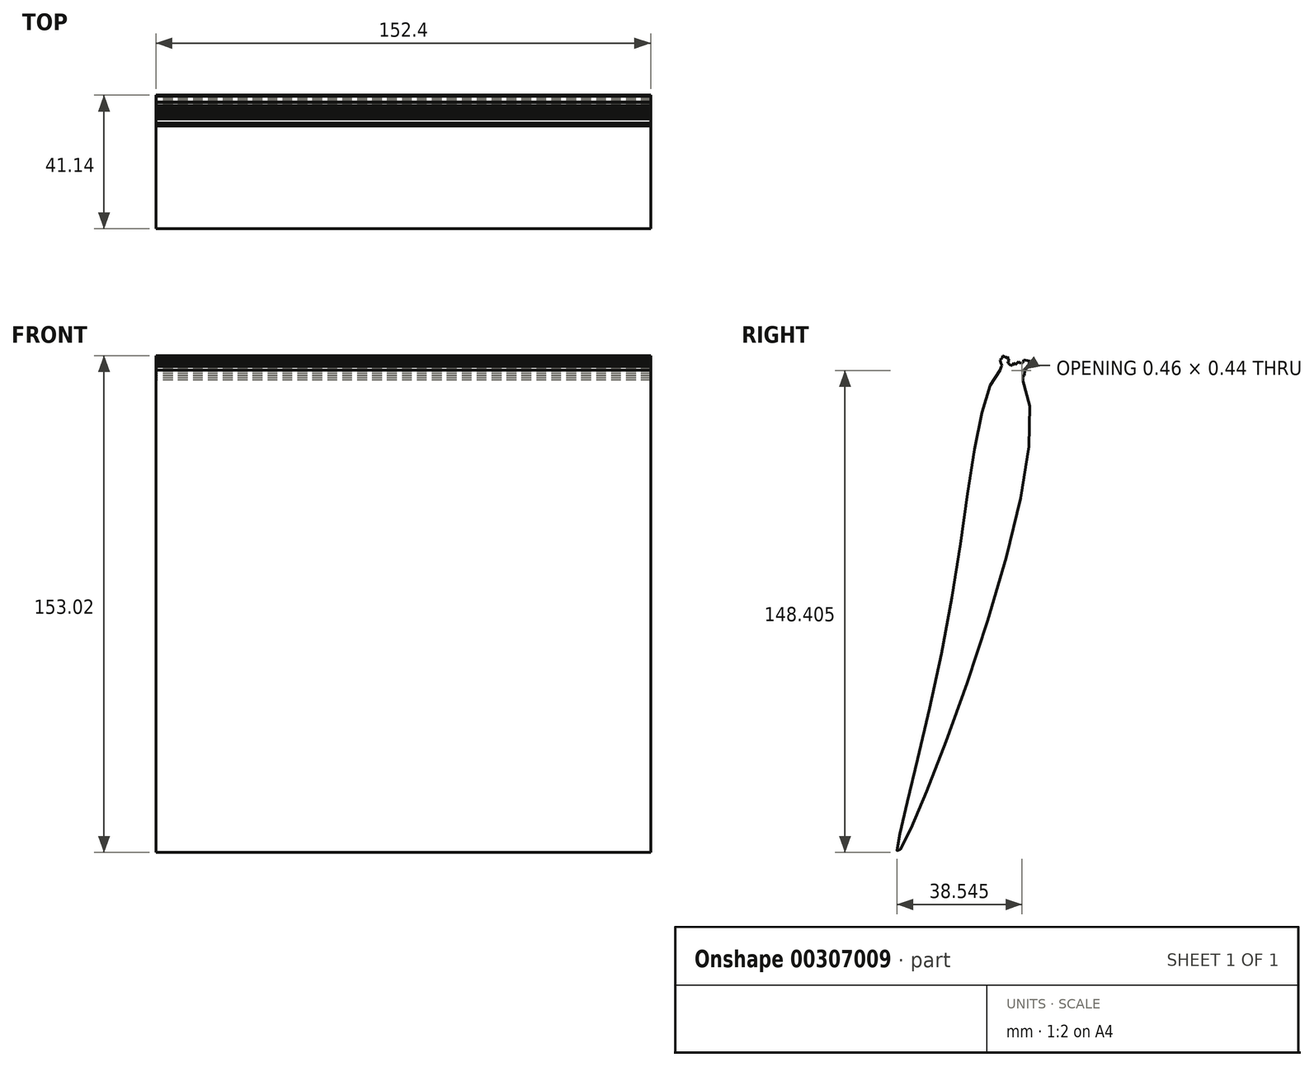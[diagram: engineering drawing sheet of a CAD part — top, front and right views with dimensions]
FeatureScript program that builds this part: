
annotation { "Feature Type Name" : "Feature", "Feature Type Description" : "" }
export const myFeature = defineFeature(function(context is Context, id is Id, definition is map)
    precondition{}
    {
        {
            var Q0;
            Q0=qCreatedBy(makeId("Right.planeOp"),FACE);
            var sketch = newSketch(context, id + "F0", { "sketchPlane" : qUnion([Q0])});
            skFitSpline(sketch, "E0", {"points": [v(29.53, 72.02) * mm, v(38.35, 56.81) * mm, v(-2.03, -76.46) * mm, v(12.04, -10.24) * mm, v(29.53, 72.02) * mm]});
            skLineSegment(sketch, "E1", {"start": v(33.62, 71.53) * mm, "end": v(36.38, 73.87) * mm});
            skLineSegment(sketch, "E2", {"start": v(36.38, 73.87) * mm, "end": v(37.28, 72.94) * mm});
            skLineSegment(sketch, "E3", {"start": v(37.28, 72.94) * mm, "end": v(34.7, 70.45) * mm});
            skLineSegment(sketch, "E4", {"start": v(34.7, 70.45) * mm, "end": v(33.62, 71.53) * mm});
            skLineSegment(sketch, "E5", {"start": v(36.38, 73.87) * mm, "end": v(37.07, 74.53) * mm});
            skPoint(sketch, "E5.endSnap0", {"position": v(36.83, 73.4) * mm});
            skLineSegment(sketch, "E6", {"start": v(37.07, 74.53) * mm, "end": v(37.91, 73.55) * mm});
            skLineSegment(sketch, "E7", {"start": v(37.91, 73.55) * mm, "end": v(37.28, 72.94) * mm});
            skLineSegment(sketch, "E8", {"start": v(31.28, 72.47) * mm, "end": v(30.78, 75.06) * mm});
            skLineSegment(sketch, "E9", {"start": v(30.78, 75.06) * mm, "end": v(29.5, 74.82) * mm});
            skLineSegment(sketch, "E10", {"start": v(29.5, 74.82) * mm, "end": v(30, 72.24) * mm});
            skLineSegment(sketch, "E11", {"start": v(30, 72.24) * mm, "end": v(31.28, 72.47) * mm});
            skLineSegment(sketch, "E12", {"start": v(35.24, 69.85) * mm, "end": v(35.54, 71.25) * mm});
            skLineSegment(sketch, "E13", {"start": v(35.54, 71.25) * mm, "end": v(36, 71.7) * mm});
            skLineSegment(sketch, "E14", {"start": v(36, 71.7) * mm, "end": v(35.94, 71.44) * mm});
            skPoint(sketch, "E14.endSnap0", {"position": v(35.77, 71.47) * mm});
            skLineSegment(sketch, "E15", {"start": v(35.94, 71.44) * mm, "end": v(35.54, 71.25) * mm});
            skLineSegment(sketch, "E16", {"start": v(35.39, 70.55) * mm, "end": v(36.12, 71.26) * mm});
            skLineSegment(sketch, "E17", {"start": v(36.12, 71.26) * mm, "end": v(36.27, 71.96) * mm});
            skLineSegment(sketch, "E18", {"start": v(36.27, 71.96) * mm, "end": v(36.66, 71.56) * mm});
            skLineSegment(sketch, "E19", {"start": v(36.66, 71.56) * mm, "end": v(36.12, 71.26) * mm});
            skLineSegment(sketch, "E20", {"start": v(36.93, 72.6) * mm, "end": v(37.75, 72.42) * mm});
            skLineSegment(sketch, "E21", {"start": v(37.75, 72.42) * mm, "end": v(37.28, 72.94) * mm});
            skLineSegment(sketch, "E22", {"start": v(37.91, 73.55) * mm, "end": v(37.84, 72.82) * mm});
            skLineSegment(sketch, "E23", {"start": v(37.84, 72.82) * mm, "end": v(37.1, 72.11) * mm});
            skLineSegment(sketch, "E24", {"start": v(37.1, 72.11) * mm, "end": v(36.27, 71.96) * mm});
            skLineSegment(sketch, "E25", {"start": v(37.1, 72.11) * mm, "end": v(37.04, 71.8) * mm});
            skLineSegment(sketch, "E26", {"start": v(37.04, 71.8) * mm, "end": v(36.66, 71.56) * mm});
            skLineSegment(sketch, "E27", {"start": v(37.84, 72.82) * mm, "end": v(37.28, 72.94) * mm});
            skLineSegment(sketch, "E28", {"start": v(36.66, 71.56) * mm, "end": v(36.46, 70.6) * mm});
            skLineSegment(sketch, "E29", {"start": v(36.46, 70.6) * mm, "end": v(35.39, 70.55) * mm});
            skLineSegment(sketch, "E30", {"start": v(37.91, 73.55) * mm, "end": v(38.08, 74.32) * mm});
            skLineSegment(sketch, "E31", {"start": v(38.08, 74.32) * mm, "end": v(37.62, 73.89) * mm});
            skLineSegment(sketch, "E32", {"start": v(37.62, 73.89) * mm, "end": v(38.08, 74.32) * mm});
            skLineSegment(sketch, "E33", {"start": v(38.08, 74.32) * mm, "end": v(37.07, 74.53) * mm});
            skLineSegment(sketch, "E34", {"start": v(37.07, 74.53) * mm, "end": v(36.27, 74.7) * mm});
            skLineSegment(sketch, "E35", {"start": v(36.27, 74.7) * mm, "end": v(36.1, 73.93) * mm});
            skLineSegment(sketch, "E36", {"start": v(36.1, 73.93) * mm, "end": v(35.1, 73.77) * mm});
            skLineSegment(sketch, "E37", {"start": v(35.1, 73.77) * mm, "end": v(34.66, 74.24) * mm});
            skLineSegment(sketch, "E38", {"start": v(34.66, 74.24) * mm, "end": v(34.42, 73.13) * mm});
            skLineSegment(sketch, "E39", {"start": v(34.42, 73.13) * mm, "end": v(34.33, 72.7) * mm});
            skLineSegment(sketch, "E40", {"start": v(34.33, 72.7) * mm, "end": v(33.6, 72.68) * mm});
            skLineSegment(sketch, "E41", {"start": v(33.6, 72.68) * mm, "end": v(33.4, 71.8) * mm});
            skLineSegment(sketch, "E42", {"start": v(33.4, 71.8) * mm, "end": v(33.62, 71.53) * mm});
            skLineSegment(sketch, "E43", {"start": v(34.66, 74.24) * mm, "end": v(33.68, 73.29) * mm});
            skLineSegment(sketch, "E44", {"start": v(33.68, 73.29) * mm, "end": v(33.16, 73.81) * mm});
            skLineSegment(sketch, "E45", {"start": v(33.16, 73.81) * mm, "end": v(32.75, 73.04) * mm});
            skLineSegment(sketch, "E46", {"start": v(32.75, 73.04) * mm, "end": v(32.05, 73.19) * mm});
            skLineSegment(sketch, "E47", {"start": v(32.05, 73.19) * mm, "end": v(31.47, 72.63) * mm});
            skLineSegment(sketch, "E48", {"start": v(32.05, 73.19) * mm, "end": v(31.51, 73.75) * mm});
            skLineSegment(sketch, "E49", {"start": v(31.51, 73.75) * mm, "end": v(31.14, 73.38) * mm});
            skLineSegment(sketch, "E50", {"start": v(31.14, 73.38) * mm, "end": v(31.31, 74.2) * mm});
            skLineSegment(sketch, "E51", {"start": v(31.31, 74.2) * mm, "end": v(30.87, 74.67) * mm});
            skLineSegment(sketch, "E52", {"start": v(30.87, 74.67) * mm, "end": v(30.78, 75.06) * mm});
            skLineSegment(sketch, "E53", {"start": v(31.31, 74.2) * mm, "end": v(31.47, 74.92) * mm});
            skLineSegment(sketch, "E54", {"start": v(31.47, 74.92) * mm, "end": v(30.87, 74.67) * mm});
            skLineSegment(sketch, "E55", {"start": v(31.47, 74.92) * mm, "end": v(31.91, 74.45) * mm});
            skLineSegment(sketch, "E56", {"start": v(31.91, 74.45) * mm, "end": v(31.31, 74.2) * mm});
            skLineSegment(sketch, "E57", {"start": v(31.47, 74.92) * mm, "end": v(31.3, 75.76) * mm});
            skLineSegment(sketch, "E58", {"start": v(31.3, 75.76) * mm, "end": v(30.78, 75.06) * mm});
            skLineSegment(sketch, "E59", {"start": v(30.78, 75.06) * mm, "end": v(30.28, 75.58) * mm});
            skPoint(sketch, "E59.endSnap0", {"position": v(30.14, 74.94) * mm});
            skLineSegment(sketch, "E60", {"start": v(30.28, 75.58) * mm, "end": v(29.5, 74.82) * mm});
            skLineSegment(sketch, "E61", {"start": v(29.5, 74.82) * mm, "end": v(29.78, 76.09) * mm});
            skLineSegment(sketch, "E62", {"start": v(29.78, 76.09) * mm, "end": v(31.04, 75.41) * mm});
            skLineSegment(sketch, "E63", {"start": v(31.04, 75.41) * mm, "end": v(31.3, 75.76) * mm});
            skLineSegment(sketch, "E64", {"start": v(29.61, 75.3) * mm, "end": v(28.98, 74.7) * mm});
            skLineSegment(sketch, "E65", {"start": v(28.98, 74.7) * mm, "end": v(29.8, 73.34) * mm});
            skLineSegment(sketch, "E66", {"start": v(29.8, 73.34) * mm, "end": v(29.18, 73.8) * mm});
            skLineSegment(sketch, "E67", {"start": v(29.18, 73.8) * mm, "end": v(29.1, 74.26) * mm});
            skLineSegment(sketch, "E68", {"start": v(29.1, 74.26) * mm, "end": v(28.98, 74.7) * mm});
            skLineSegment(sketch, "E69", {"start": v(30, 72.24) * mm, "end": v(29.53, 72.02) * mm});
            skLineSegment(sketch, "E70", {"start": v(29.53, 72.02) * mm, "end": v(29.4, 72.7) * mm});
            skLineSegment(sketch, "E71", {"start": v(29.4, 72.7) * mm, "end": v(29.86, 73.24) * mm});
            skLineSegment(sketch, "E72", {"start": v(29.86, 73.24) * mm, "end": v(29.18, 73.8) * mm});
            skLineSegment(sketch, "E73", {"start": v(29.18, 73.8) * mm, "end": v(29.63, 72.97) * mm});
            skLineSegment(sketch, "E74", {"start": v(36.46, 70.6) * mm, "end": v(36.5, 69.9) * mm});
            skLineSegment(sketch, "E75", {"start": v(36.5, 69.9) * mm, "end": v(35.97, 69.82) * mm});
            skLineSegment(sketch, "E76", {"start": v(35.97, 69.82) * mm, "end": v(36.07, 69.2) * mm});
            skLineSegment(sketch, "E77", {"start": v(36.07, 69.2) * mm, "end": v(35.93, 68.54) * mm});
            skLineSegment(sketch, "E78", {"start": v(35.93, 68.54) * mm, "end": v(35.24, 69.85) * mm});
            skLineSegment(sketch, "E79", {"start": v(29.4, 72.7) * mm, "end": v(28.93, 71.6) * mm});
            skLineSegment(sketch, "E80", {"start": v(28.93, 71.6) * mm, "end": v(29.53, 72.02) * mm});
            skLineSegment(sketch, "E81", {"start": v(31.31, 74.2) * mm, "end": v(31.51, 73.75) * mm});
            skLineSegment(sketch, "E82.0", {"start": v(29.4, 72.7) * mm, "end": v(36.12, 71.26) * mm, "construction": true});
            skLineSegment(sketch, "E83.0", {"start": v(29.1, 74.26) * mm, "end": v(37.75, 72.42) * mm, "construction": true});
            skLineSegment(sketch, "E84.0", {"start": v(29.18, 73.8) * mm, "end": v(32.05, 73.19) * mm, "construction": true});
            skLineSegment(sketch, "E85.0", {"start": v(29.8, 73.34) * mm, "end": v(37.04, 71.8) * mm, "construction": true});
            skLineSegment(sketch, "E86.0", {"start": v(28.98, 74.7) * mm, "end": v(37.84, 72.82) * mm, "construction": true});
            skLineSegment(sketch, "E87.0", {"start": v(29.78, 76.09) * mm, "end": v(38.08, 74.32) * mm, "construction": true});
            skLineSegment(sketch, "E88.0", {"start": v(29.61, 75.3) * mm, "end": v(37.91, 73.55) * mm, "construction": true});
            skLineSegment(sketch, "E89.0", {"start": v(30.87, 74.67) * mm, "end": v(36.83, 73.4) * mm, "construction": true});
            skLineSegment(sketch, "E90.0", {"start": v(35.77, 71.47) * mm, "end": v(35.94, 71.44) * mm, "construction": true});
            skLineSegment(sketch, "E91.0", {"start": v(33.68, 73.29) * mm, "end": v(34.42, 73.13) * mm, "construction": true});
            skLineSegment(sketch, "E92.0", {"start": v(34.33, 72.7) * mm, "end": v(37.1, 72.11) * mm, "construction": true});
            skLineSegment(sketch, "E93.0", {"start": v(29.8, 73.34) * mm, "end": v(30.28, 75.58) * mm, "construction": true});
            skLineSegment(sketch, "E94.0", {"start": v(37.1, 72.11) * mm, "end": v(37.28, 72.94) * mm, "construction": true});
            skLineSegment(sketch, "E95.0", {"start": v(29.5, 74.82) * mm, "end": v(29.61, 75.3) * mm, "construction": true});
            skLineSegment(sketch, "E96.0", {"start": v(36.83, 73.4) * mm, "end": v(37.07, 74.53) * mm, "construction": true});
            skLineSegment(sketch, "E97.0", {"start": v(35.39, 70.55) * mm, "end": v(36.27, 74.7) * mm, "construction": true});
            skLineSegment(sketch, "E98.0", {"start": v(37.75, 72.42) * mm, "end": v(37.84, 72.82) * mm, "construction": true});
            skSolve(sketch);
        }
        {
            var Q0;
            Q0=qSketchRegion(id+"F0",true);
            var Q1;
            Q1=makeQuery(id+"F0.imprint","IMPRINT",FACE,{"disambiguationData":[TD([[makeQuery(id+"F0.imprint","IMPRINT",EDGE,{"derivedFrom":sQuery(id+"F0.wireOp",EDGE,"E1")}),1.0]])]});
            var Q2;
            {var subQ3=sQuery(id+"F0.wireOp",EDGE,"E1");Q2=makeQuery(id+"F0.imprint","IMPRINT",FACE,{"disambiguationData":[TD([[makeQuery(id+"F0.imprint","IMPRINT",EDGE,{"derivedFrom":subQ3}),-1.0]])]});}
            var Q3;
            {var subQ0=sQuery(id+"F0.wireOp",EDGE,"E29");Q3=makeQuery(id+"F0.imprint","IMPRINT",FACE,{"disambiguationData":[TD([[makeQuery(id+"F0.imprint","IMPRINT",EDGE,{"derivedFrom":subQ0}),1.0]])]});}
            var Q4;
            {var subQ0=sQuery(id+"F0.wireOp",EDGE,"E78");var subQ1=sQuery(id+"F0.wireOp",EDGE,"E12");var subQ2=makeQuery(id+"F0.imprint","INTERSECT",VERTEX,{"derivedFrom":[subQ1,subQ0]});Q4=makeQuery(id+"F0.imprint","IMPRINT",FACE,{"disambiguationData":[TD([[makeQuery(id+"F0.imprint","IMPRINT",EDGE,{"disambiguationData":[TD([[subQ2,1.0]])],"derivedFrom":subQ0}),1.0]])]});}
            var Q5;
            {var subQ2=sQuery(id+"F0.wireOp",EDGE,"E8");Q5=makeQuery(id+"F0.imprint","IMPRINT",FACE,{"disambiguationData":[TD([[makeQuery(id+"F0.imprint","IMPRINT",EDGE,{"derivedFrom":subQ2}),-1.0]])]});}
            var Q6;
            {var subQ0=sQuery(id+"F0.wireOp",EDGE,"E11");Q6=makeQuery(id+"F0.imprint","IMPRINT",FACE,{"disambiguationData":[TD([[makeQuery(id+"F0.imprint","IMPRINT",EDGE,{"derivedFrom":subQ0}),1.0]])]});}
            var Q7;
            {var subQ0=sQuery(id+"F0.wireOp",EDGE,"E4");Q7=makeQuery(id+"F0.imprint","IMPRINT",FACE,{"disambiguationData":[TD([[makeQuery(id+"F0.imprint","IMPRINT",EDGE,{"derivedFrom":subQ0}),-1.0]])]});}
            var Q8;
            {var subQ0=sQuery(id+"F0.wireOp",EDGE,"E78");var subQ1=sQuery(id+"F0.wireOp",EDGE,"E0");var subQ3=makeQuery(id+"F0.imprint","INTERSECT",VERTEX,{"derivedFrom":[subQ1,subQ0]});Q8=makeQuery(id+"F0.imprint","IMPRINT",FACE,{"disambiguationData":[TD([[makeQuery(id+"F0.imprint","IMPRINT",EDGE,{"disambiguationData":[TD([[subQ3,-1.0]])],"derivedFrom":subQ1}),-1.0]])]});}
            var Q9;
            {var subQ6=sQuery(id+"F0.wireOp",EDGE,"E8");Q9=makeQuery(id+"F0.imprint","IMPRINT",FACE,{"disambiguationData":[TD([[makeQuery(id+"F0.imprint","IMPRINT",EDGE,{"derivedFrom":subQ6}),1.0]])]});}
            var Q10;
            Q10=makeQuery(id+"F0.imprint","IMPRINT",FACE,{"disambiguationData":[TD([[makeQuery(id+"F0.imprint","IMPRINT",EDGE,{"derivedFrom":sQuery(id+"F0.wireOp",EDGE,"E58")}),-1.0]])]});
            var Q11;
            {var subQ0=sQuery(id+"F0.wireOp",EDGE,"E69");Q11=makeQuery(id+"F0.imprint","IMPRINT",FACE,{"disambiguationData":[TD([[makeQuery(id+"F0.imprint","IMPRINT",EDGE,{"derivedFrom":subQ0}),-1.0]])]});}
            var Q12;
            {var subQ1=sQuery(id+"F0.wireOp",EDGE,"E70");Q12=makeQuery(id+"F0.imprint","IMPRINT",FACE,{"disambiguationData":[TD([[makeQuery(id+"F0.imprint","IMPRINT",EDGE,{"derivedFrom":subQ1}),1.0]])]});}
            var Q13;
            {var subQ0=sQuery(id+"F0.wireOp",EDGE,"E80");Q13=makeQuery(id+"F0.imprint","IMPRINT",FACE,{"disambiguationData":[TD([[makeQuery(id+"F0.imprint","IMPRINT",EDGE,{"derivedFrom":subQ0}),1.0]])]});}
            var Q14;
            {var subQ5=sQuery(id+"F0.wireOp",EDGE,"E64");Q14=makeQuery(id+"F0.imprint","IMPRINT",FACE,{"disambiguationData":[TD([[makeQuery(id+"F0.imprint","IMPRINT",EDGE,{"derivedFrom":subQ5}),1.0]])]});}
            var Q15;
            {var subQ1=sQuery(id+"F0.wireOp",EDGE,"E70");Q15=makeQuery(id+"F0.imprint","IMPRINT",FACE,{"disambiguationData":[TD([[makeQuery(id+"F0.imprint","IMPRINT",EDGE,{"derivedFrom":subQ1}),-1.0]])]});}
            var Q16;
            {var subQ0=sQuery(id+"F0.wireOp",EDGE,"E67");Q16=makeQuery(id+"F0.imprint","IMPRINT",FACE,{"disambiguationData":[TD([[makeQuery(id+"F0.imprint","IMPRINT",EDGE,{"derivedFrom":subQ0}),-1.0]])]});}
            var Q17;
            {var subQ0=sQuery(id+"F0.wireOp",EDGE,"E72");var subQ1=sQuery(id+"F0.wireOp",EDGE,"E10");var subQ2=makeQuery(id+"F0.imprint","INTERSECT",VERTEX,{"derivedFrom":[subQ1,subQ0]});Q17=makeQuery(id+"F0.imprint","IMPRINT",FACE,{"disambiguationData":[TD([[makeQuery(id+"F0.imprint","IMPRINT",EDGE,{"disambiguationData":[TD([[subQ2,-1.0]])],"derivedFrom":subQ1}),1.0]])]});}
            var Q18;
            Q18=makeQuery(id+"F0.imprint","IMPRINT",FACE,{"disambiguationData":[TD([[makeQuery(id+"F0.imprint","IMPRINT",EDGE,{"derivedFrom":sQuery(id+"F0.wireOp",EDGE,"E9")}),-1.0]])]});
            var Q19;
            Q19=makeQuery(id+"F0.imprint","IMPRINT",FACE,{"disambiguationData":[TD([[makeQuery(id+"F0.imprint","IMPRINT",EDGE,{"derivedFrom":sQuery(id+"F0.wireOp",EDGE,"E17")}),-1.0]])]});
            var Q20;
            {var subQ0=sQuery(id+"F0.wireOp",EDGE,"E65");var subQ1=sQuery(id+"F0.wireOp",EDGE,"E10");var subQ2=makeQuery(id+"F0.imprint","INTERSECT",VERTEX,{"derivedFrom":[subQ1,subQ0]});Q20=makeQuery(id+"F0.imprint","IMPRINT",FACE,{"disambiguationData":[TD([[makeQuery(id+"F0.imprint","IMPRINT",EDGE,{"disambiguationData":[TD([[subQ2,-1.0]])],"derivedFrom":subQ1}),1.0]])]});}
            var Q21;
            Q21=makeQuery(id+"F0.imprint","IMPRINT",FACE,{"disambiguationData":[TD([[makeQuery(id+"F0.imprint","IMPRINT",EDGE,{"derivedFrom":sQuery(id+"F0.wireOp",EDGE,"E18")}),1.0]])]});
            var Q22;
            Q22=makeQuery(id+"F0.imprint","IMPRINT",FACE,{"disambiguationData":[TD([[makeQuery(id+"F0.imprint","IMPRINT",EDGE,{"derivedFrom":sQuery(id+"F0.wireOp",EDGE,"E49")}),-1.0]])]});
            var Q23;
            {var subQ2=sQuery(id+"F0.wireOp",EDGE,"E32");Q23=makeQuery(id+"F0.imprint","IMPRINT",FACE,{"disambiguationData":[TD([[makeQuery(id+"F0.imprint","IMPRINT",EDGE,{"derivedFrom":subQ2}),1.0]])]});}
            var Q24;
            {var subQ0=sQuery(id+"F0.wireOp",EDGE,"E66");var subQ1=sQuery(id+"F0.wireOp",EDGE,"E10");var subQ2=makeQuery(id+"F0.imprint","INTERSECT",VERTEX,{"derivedFrom":[subQ1,subQ0]});Q24=makeQuery(id+"F0.imprint","IMPRINT",FACE,{"disambiguationData":[TD([[makeQuery(id+"F0.imprint","IMPRINT",EDGE,{"disambiguationData":[TD([[subQ2,-1.0]])],"derivedFrom":subQ1}),-1.0]])]});}
            var Q25;
            Q25=makeQuery(id+"F0.imprint","IMPRINT",FACE,{"disambiguationData":[TD([[makeQuery(id+"F0.imprint","IMPRINT",EDGE,{"derivedFrom":sQuery(id+"F0.wireOp",EDGE,"E2")}),1.0]])]});
            var Q26;
            {var subQ5=sQuery(id+"F0.wireOp",EDGE,"E73");Q26=makeQuery(id+"F0.imprint","IMPRINT",FACE,{"disambiguationData":[TD([[makeQuery(id+"F0.imprint","IMPRINT",EDGE,{"derivedFrom":subQ5}),1.0]])]});}
            var Q27;
            {var subQ1=sQuery(id+"F0.wireOp",EDGE,"E14");Q27=makeQuery(id+"F0.imprint","IMPRINT",FACE,{"disambiguationData":[TD([[makeQuery(id+"F0.imprint","IMPRINT",EDGE,{"derivedFrom":subQ1}),1.0]])]});}
            var Q28;
            Q28=makeQuery(id+"F0.imprint","IMPRINT",FACE,{"disambiguationData":[TD([[makeQuery(id+"F0.imprint","IMPRINT",EDGE,{"derivedFrom":sQuery(id+"F0.wireOp",EDGE,"E16")}),-1.0]])]});
            var Q29;
            {var subQ0=sQuery(id+"F0.wireOp",EDGE,"E24");Q29=makeQuery(id+"F0.imprint","IMPRINT",FACE,{"disambiguationData":[TD([[makeQuery(id+"F0.imprint","IMPRINT",EDGE,{"derivedFrom":subQ0}),-1.0]])]});}
            var Q30;
            Q30=makeQuery(id+"F0.imprint","IMPRINT",FACE,{"disambiguationData":[TD([[makeQuery(id+"F0.imprint","IMPRINT",EDGE,{"derivedFrom":sQuery(id+"F0.wireOp",EDGE,"E13")}),-1.0]])]});
            var Q31;
            {var subQ0=sQuery(id+"F0.wireOp",EDGE,"E21");var subQ1=sQuery(id+"F0.wireOp",EDGE,"E20");var subQ2=makeQuery(id+"F0.imprint","INTERSECT",VERTEX,{"derivedFrom":[subQ1,subQ0]});Q31=makeQuery(id+"F0.imprint","IMPRINT",FACE,{"disambiguationData":[TD([[makeQuery(id+"F0.imprint","IMPRINT",EDGE,{"disambiguationData":[TD([[subQ2,1.0]])],"derivedFrom":subQ1}),1.0]])]});}
            var Q32;
            Q32=makeQuery(id+"F0.imprint","IMPRINT",FACE,{"disambiguationData":[TD([[makeQuery(id+"F0.imprint","IMPRINT",EDGE,{"derivedFrom":sQuery(id+"F0.wireOp",EDGE,"E53")}),-1.0]])]});
            var Q33;
            {var subQ0=sQuery(id+"F0.wireOp",EDGE,"E30");Q33=makeQuery(id+"F0.imprint","IMPRINT",FACE,{"disambiguationData":[TD([[makeQuery(id+"F0.imprint","IMPRINT",EDGE,{"derivedFrom":subQ0}),1.0]])]});}
            var Q34;
            Q34=makeQuery(id+"F0.imprint","IMPRINT",FACE,{"disambiguationData":[TD([[makeQuery(id+"F0.imprint","IMPRINT",EDGE,{"derivedFrom":sQuery(id+"F0.wireOp",EDGE,"E7")}),1.0]])]});
            var Q35;
            Q35=makeQuery(id+"F0.imprint","IMPRINT",FACE,{"disambiguationData":[TD([[makeQuery(id+"F0.imprint","IMPRINT",EDGE,{"derivedFrom":sQuery(id+"F0.wireOp",EDGE,"E51")}),-1.0]])]});
            var Q36;
            Q36=makeQuery(id+"F0.imprint","IMPRINT",FACE,{"disambiguationData":[TD([[makeQuery(id+"F0.imprint","IMPRINT",EDGE,{"derivedFrom":sQuery(id+"F0.wireOp",EDGE,"E52")}),-1.0]])]});
            var Q37;
            {var subQ1=sQuery(id+"F0.wireOp",EDGE,"E3");var subQ3=sQuery(id+"F0.wireOp",EDGE,"E20");var subQ4=makeQuery(id+"F0.imprint","INTERSECT",VERTEX,{"derivedFrom":[subQ1,subQ3]});Q37=makeQuery(id+"F0.imprint","IMPRINT",FACE,{"disambiguationData":[TD([[makeQuery(id+"F0.imprint","IMPRINT",EDGE,{"disambiguationData":[TD([[subQ4,-1.0]])],"derivedFrom":subQ3}),1.0]])]});}
            var Q38;
            {var subQ0=sQuery(id+"F0.wireOp",EDGE,"E27");Q38=makeQuery(id+"F0.imprint","IMPRINT",FACE,{"disambiguationData":[TD([[makeQuery(id+"F0.imprint","IMPRINT",EDGE,{"derivedFrom":subQ0}),1.0]])]});}
            var Q39;
            {var subQ4=sQuery(id+"F0.wireOp",EDGE,"E4");Q39=makeQuery(id+"F0.imprint","IMPRINT",FACE,{"disambiguationData":[TD([[makeQuery(id+"F0.imprint","IMPRINT",EDGE,{"derivedFrom":subQ4}),1.0]])]});}
            extrude(context, id + "F1", {"entities" : qUnion([Q0, Q1, Q2, Q3, Q4, Q5, Q6, Q7, Q8, Q9, Q10, Q11, Q12, Q13, Q14, Q15, Q16, Q17, Q18, Q19, Q20, Q21, Q22, Q23, Q24, Q25, Q26, Q27, Q28, Q29, Q30, Q31, Q32, Q33, Q34, Q35, Q36, Q37, Q38, Q39]), "depth" : 76.2 * mm, "hasSecondDirection" : true, "secondDirectionOppositeDirection" : true, "secondDirectionDepth" : 76.2 * mm});
        }
    });
